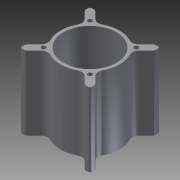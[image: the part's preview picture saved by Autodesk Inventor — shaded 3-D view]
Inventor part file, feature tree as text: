
AUTODESK INVENTOR PART (.ipt)
format: ipt  version: 2012 SP2 (Build 160219200, 219)  size: 219,136 bytes
history: native  units: mm
features: extrude x3, sketch x3
ambient origin geometry x8: Origin, YZ Plane, XZ Plane, XY Plane, X Axis, Y Axis, Z Axis, Center Point
bodies: Solid1 (feature_tree)
feature tree (6):
  extrude  "Extrusion1"  Depth=250.0mm TaperAngle=0.0deg
  extrude  "Extrusion2"  Depth=102.676337mm
  extrude  "Extrusion3"  Depth=95.0mm TaperAngle=0.0deg
  sketch  "Sketch1"  dims[d0=400.0mm d1=0.0mm d2=250.0mm d3=0.0mm]
  sketch  "Sketch2"  dims[d4=50.0mm d5=102.676337mm]
  sketch  "Sketch3"  dims[d6=3.004552mm d7=95.0mm d8=0.0mm]
